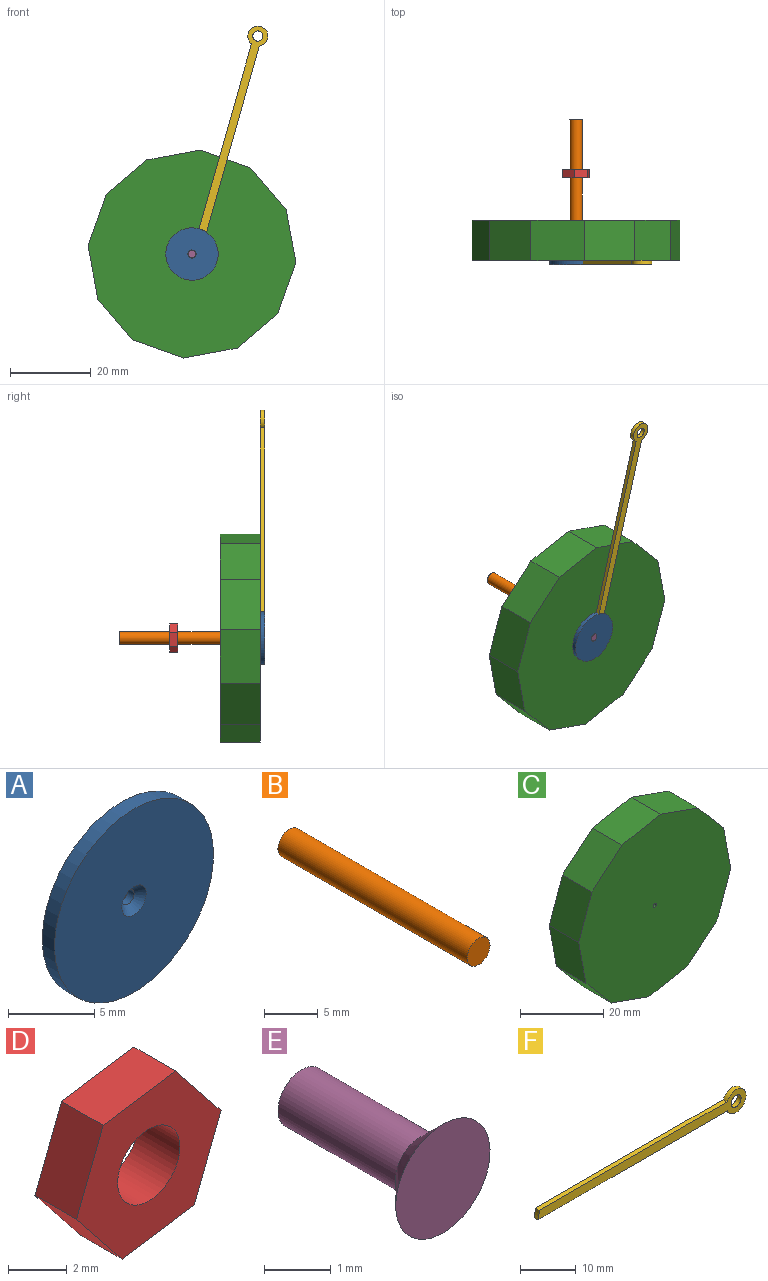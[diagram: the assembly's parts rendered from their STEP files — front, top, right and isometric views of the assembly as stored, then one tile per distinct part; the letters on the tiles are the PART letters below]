
ASSEMBLY  parts=6 mates=6
PART A: 5 faces, bbox 13x1x13 mm
  f0: cylinder r=6.5mm len=13mm, axis (0,1,0), area 40.8mm2, adj f1,f2
  f1: plane 13x13mm, normal (0,-1,0), area 129.6mm2, adj f0,f4
  f2: plane 13x13mm, normal (0,1,0), area 131.9mm2, adj f0,f3
  f3: cylinder r=0.5mm len=1mm, axis (0,-1,0), area 1.6mm2, adj f2,f4
  f4: cone r=0.5mm half-angle=45deg, axis (0,-1,0), area 3.3mm2, adj f1,f3
PART B: 3 faces, bbox 3x25x3 mm
  f0: cylinder r=1.5mm len=25mm, axis (0,1,0), area 235.6mm2, adj f1,f2
  f1: plane 3x3mm, normal (0,-1,0), area 7.1mm2, adj f0
  f2: plane 3x3mm, normal (0,1,0), area 7.1mm2, adj f0
PART C: 16 faces, bbox 51.6x10x51.6 mm
  f0: plane 10.18x10mm, normal (-0.65,0,0.76), area 134mm2, adj f1,f11,f12,f13
  f1: plane 12.63x10mm, normal (-0.94,0,0.33), area 134mm2, adj f0,f2,f12,f13
  f2: plane 13.17x10mm, normal (-0.98,0,-0.18), area 134mm2, adj f1,f3,f12,f13
  f3: plane 10.18x10mm, normal (-0.76,0,-0.65), area 134mm2, adj f2,f4,f12,f13
  f4: plane 12.63x10mm, normal (-0.33,0,-0.94), area 134mm2, adj f3,f5,f12,f13
  f5: plane 13.17x10mm, normal (0.18,0,-0.98), area 134mm2, adj f4,f6,f12,f13
  f6: plane 10.18x10mm, normal (0.65,0,-0.76), area 134mm2, adj f5,f7,f12,f13
  f7: plane 12.63x10mm, normal (0.94,0,-0.33), area 134mm2, adj f6,f8,f12,f13
  f8: plane 13.17x10mm, normal (0.98,0,0.18), area 134mm2, adj f7,f9,f12,f13
  f9: plane 10.18x10mm, normal (0.76,0,0.65), area 134mm2, adj f8,f10,f12,f13
  f10: plane 12.63x10mm, normal (0.33,0,0.94), area 134mm2, adj f9,f11,f12,f13
  f11: plane 13.17x10mm, normal (-0.18,0,0.98), area 134mm2, adj f0,f10,f12,f13
  f12: plane 51.61x51.61mm, normal (0,-1,0), area 2008.8mm2, adj f0,f1,f2,f3,f4,f5,f6,f7
  f13: plane 51.61x51.61mm, normal (0,1,0), area 2009.6mm2, adj f0,f1,f2,f3,f4,f5,f6,f7
  f14: cone r=0mm half-angle=59deg, axis (0,-1,0), area 0.9mm2, adj f15
  f15: cylinder r=0.5mm len=2mm, axis (0,-1,0), area 6.3mm2, adj f12,f14
PART D: 9 faces, bbox 7x2x6.6 mm
  f0: plane 2.76x2.2mm, normal (0.78,0,0.62), area 7mm2, adj f1,f6,f7,f8
  f1: plane 3.49x2mm, normal (-0.15,0,0.99), area 7mm2, adj f0,f2,f7,f8
  f2: plane 3.28x2mm, normal (-0.93,0,0.36), area 7mm2, adj f1,f3,f7,f8
  f3: plane 2.76x2.2mm, normal (-0.78,0,-0.62), area 7mm2, adj f2,f4,f7,f8
  f4: plane 3.49x2mm, normal (0.15,0,-0.99), area 7mm2, adj f3,f6,f7,f8
  f5: cylinder r=1.5mm len=3mm, axis (0,1,0), area 18.8mm2, adj f7,f8
  f6: plane 3.28x2mm, normal (0.93,0,-0.36), area 7mm2, adj f0,f4,f7,f8
  f7: plane 6.97x6.56mm, normal (0,-1,0), area 25.2mm2, adj f0,f1,f2,f3,f4,f5,f6
  f8: plane 6.97x6.56mm, normal (0,1,0), area 25.2mm2, adj f0,f1,f2,f3,f4,f5,f6
PART E: 4 faces, bbox 2x3.3x2 mm
  f0: plane 2x2mm, normal (0,-1,0), area 3.1mm2, adj f1
  f1: cone r=0.5mm half-angle=45deg, axis (0,-1,0), area 3.3mm2, adj f0,f3
  f2: cone r=0mm half-angle=59deg, axis (0,-1,0), area 0.9mm2, adj f3
  f3: cylinder r=0.5mm len=2.5mm, axis (0,-1,0), area 7.9mm2, adj f1,f2
PART F: 7 faces, bbox 52.8x1x5 mm
  f0: cylinder r=6.5mm len=1.97mm, axis (0,1,0), area 2mm2, adj f1,f3,f5,f6
  f1: plane 48.01x1mm, normal (0,0,-1), area 48mm2, adj f0,f2,f5,f6
  f2: cylinder r=2.5mm len=5mm, axis (0,1,0), area 13.7mm2, adj f1,f3,f5,f6
  f3: plane 47.7x1mm, normal (0,0,1), area 47.7mm2, adj f0,f2,f5,f6
  f4: cylinder r=1.27mm len=2.54mm, axis (0,1,0), area 8mm2, adj f5,f6
  f5: plane 52.81x5mm, normal (0,-1,0), area 108.5mm2, adj f0,f1,f2,f3,f4
  f6: plane 52.81x5mm, normal (0,1,0), area 108.5mm2, adj f0,f1,f2,f3,f4
PLACE A rot(axis=(0,-1,0),74.2deg) t=(0,0,0)mm
PLACE B t=(9.24,35,-16.57)mm
PLACE C at identity fixed
PLACE D rot(axis=(0,1,0),150.7deg) t=(-16.17,22.5,9.92)mm
PLACE E rot(axis=(0,1,0),15.8deg) t=(0,0,0)mm
PLACE F rot(axis=(0,-1,0),74.2deg) t=(0,0,0)mm
MATE cylindrical B.f0 <-> D.f5  axis (0,1,0) through (0,12.5,0)mm
MATE revolute C.f14 <-> A.f0  axis (0,-1,0) through (0,-10,0)mm
MATE fastened A.f0 <-> F.f0  axis (0,1,0) through (0,-10.5,0)mm
MATE fastened C.f14 <-> B.f0  axis (0,1,0) through (0,0,0)mm
MATE fastened A.f0 <-> E.f1  axis (0,-1,0) through (0,-11,0)mm
MATE planar D.f5 <-> B.f0  axis (0,1,0) through (0,12.5,0)mm
